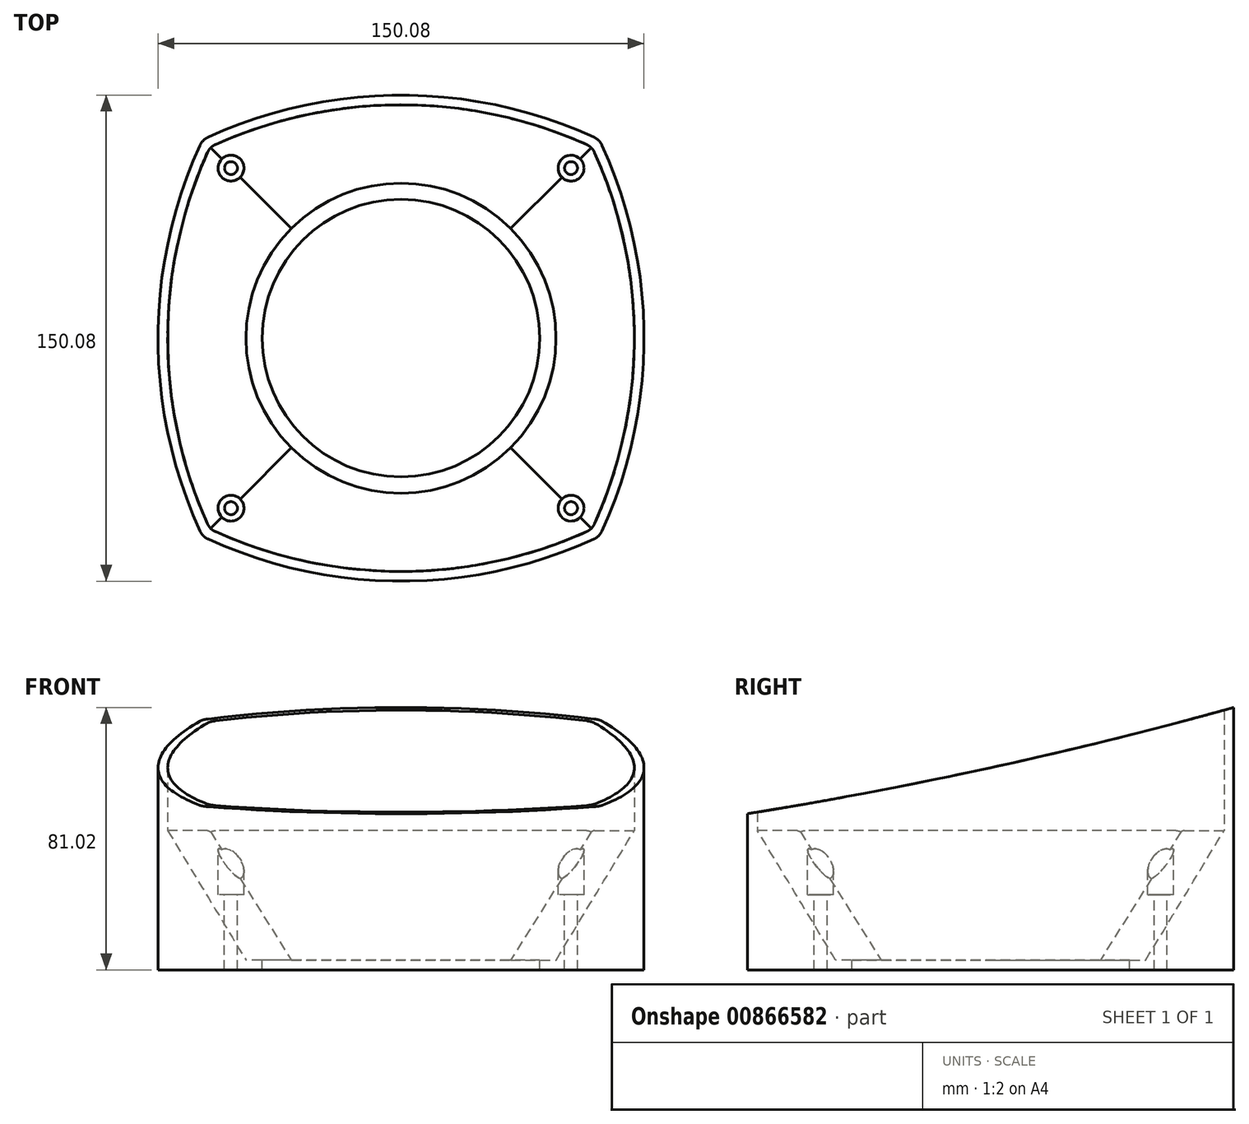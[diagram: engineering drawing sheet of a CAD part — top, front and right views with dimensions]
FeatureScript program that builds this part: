
annotation { "Feature Type Name" : "Feature", "Feature Type Description" : "" }
export const myFeature = defineFeature(function(context is Context, id is Id, definition is map)
    precondition{}
    {
        {
            var Q0;
            Q0=qCreatedBy(makeId("Top.planeOp"),FACE);
            var sketch = newSketch(context, id + "F0", { "sketchPlane" : qUnion([Q0])});
            skLineSegment(sketch, "E0.bottom", {"start": v(196, 49) * mm, "end": v(-196, 49) * mm, "construction": true});
            skLineSegment(sketch, "E0.top", {"start": v(196, -49) * mm, "end": v(-196, -49) * mm, "construction": true});
            skLineSegment(sketch, "E0.left", {"start": v(196, 49) * mm, "end": v(196, -49) * mm, "construction": true});
            skLineSegment(sketch, "E0.right", {"start": v(-196, 49) * mm, "end": v(-196, -49) * mm, "construction": true});
            skPoint(sketch, "E0.middle", {"position": v(0, 0) * mm});
            skLineSegment(sketch, "E1.bottom", {"start": v(207, 59) * mm, "end": v(-207, 59) * mm, "construction": true});
            skLineSegment(sketch, "E1.top", {"start": v(207, -59) * mm, "end": v(-207, -59) * mm, "construction": true});
            skLineSegment(sketch, "E1.left", {"start": v(207, 59) * mm, "end": v(207, -59) * mm, "construction": true});
            skLineSegment(sketch, "E1.right", {"start": v(-207, 59) * mm, "end": v(-207, -59) * mm, "construction": true});
            skLineSegment(sketch, "E2", {"start": v(0, -59) * mm, "end": v(0, 59) * mm, "construction": true});
            skLineSegment(sketch, "E3", {"start": v(-207, 0) * mm, "end": v(207, 0) * mm, "construction": true});
            skCircle(sketch, "E4", {"center": v(0, 0) * mm, "radius": 47.86 * mm});
            skLineSegment(sketch, "E5.bottom", {"start": v(59, 59) * mm, "end": v(-59, 59) * mm, "construction": true});
            skLineSegment(sketch, "E5.top", {"start": v(59, -59) * mm, "end": v(-59, -59) * mm, "construction": true});
            skLineSegment(sketch, "E5.left", {"start": v(59, 59) * mm, "end": v(59, -59) * mm, "construction": true});
            skLineSegment(sketch, "E5.right", {"start": v(-59, 59) * mm, "end": v(-59, -59) * mm, "construction": true});
            skArc(sketch, "E6", {"start": v(59, 59) * mm, "mid": v(0, 72.04) * mm, "end": v(-59, 59) * mm});
            skArc(sketch, "E7", {"start": v(59, -59) * mm, "mid": v(72.04, 0) * mm, "end": v(59, 59) * mm});
            skArc(sketch, "E8", {"start": v(-59, -59) * mm, "mid": v(0, -72.04) * mm, "end": v(59, -59) * mm});
            skArc(sketch, "E9", {"start": v(-59, 59) * mm, "mid": v(-72.04, 0) * mm, "end": v(-59, -59) * mm});
            skArc(sketch, "E10.0", {"start": v(61.26, 61.26) * mm, "mid": v(0, 75.04) * mm, "end": v(-61.26, 61.26) * mm});
            skArc(sketch, "E10.1", {"start": v(61.26, -61.26) * mm, "mid": v(75.04, 0) * mm, "end": v(61.26, 61.26) * mm});
            skArc(sketch, "E10.2", {"start": v(-61.26, -61.26) * mm, "mid": v(0, -75.04) * mm, "end": v(61.26, -61.26) * mm});
            skArc(sketch, "E10.3", {"start": v(-61.26, 61.26) * mm, "mid": v(-75.04, 0) * mm, "end": v(-61.26, -61.26) * mm});
            skSolve(sketch);
        }
        {
            var Q0;
            {var subQ8=sQuery(id+"F0.wireOp",EDGE,"E6");Q0=makeQuery(id+"F0.imprint","IMPRINT",FACE,{"disambiguationData":[TD([[makeQuery(id+"F0.imprint","IMPRINT",EDGE,{"derivedFrom":subQ8}),-1.0]])]});}
            var Q1;
            {var subQ0=sQuery(id+"F0.wireOp",EDGE,"E10.1");var subQ1=sQuery(id+"F0.wireOp",EDGE,"2c3d49d2-39e6-4b7c-b00d-7af9e24e8e71.0");var subQ2=makeQuery(id+"F0.imprint","INTERSECT",VERTEX,{"disambiguationData":[OD(0.0)],"derivedFrom":[subQ1,subQ0]});Q1=makeQuery(id+"F0.imprint","IMPRINT",FACE,{"disambiguationData":[TD([[makeQuery(id+"F0.imprint","IMPRINT",EDGE,{"disambiguationData":[TD([[subQ2,-1.0]])],"derivedFrom":subQ1}),1.0]])]});}
            extrude(context, id + "F1", {"entities" : qUnion([Q0, Q1]), "endBound" : BoundingType.SYMMETRIC, "depth" : 160 * mm, "offsetDistance" : 25 * mm});
        }
        {
            var Q0;
            Q0=qCreatedBy(makeId("Right.planeOp"),FACE);
            var sketch = newSketch(context, id + "F2", { "sketchPlane" : qUnion([Q0])});
            skCircle(sketch, "E11", {"center": v(-294.04, 1407.06) * mm, "radius": 1379.34 * mm});
            skLineSegment(sketch, "E12", {"start": v(0, 0) * mm, "end": v(-237.77, 0) * mm, "construction": true});
            skCircle(sketch, "E13.MirrorC", {"center": v(-294.04, -1407.06) * mm, "radius": 1379.34 * mm});
            skSolve(sketch);
        }
        {
            var Q0;
            Q0=makeQuery(id+"F2.imprint","IMPRINT",FACE,{"disambiguationData":[TD([[makeQuery(id+"F2.imprint","IMPRINT",EDGE,{"derivedFrom":sQuery(id+"F2.wireOp",EDGE,"E11")}),1.0]])]});
            var Q1;
            Q1=makeQuery(id+"F2.imprint","IMPRINT",FACE,{"disambiguationData":[TD([[makeQuery(id+"F2.imprint","IMPRINT",EDGE,{"derivedFrom":sQuery(id+"F2.wireOp",EDGE,"E13.MirrorC")}),-1.0]])]});
            extrude(context, id + "F3", {"entities" : qUnion([Q0, Q1]), "operationType" : NewBodyOperationType.REMOVE, "endBound" : BoundingType.SYMMETRIC, "oppositeDirection" : true, "depth" : 780 * mm, "offsetDistance" : 25 * mm});
        }
        {
            var Q0;
            Q0=qCreatedBy(makeId("Top.planeOp"),FACE);
            cPlane(context, id + "F4", {"entities" : qUnion([Q0]), "cplaneType" : CPlaneType.OFFSET, "offset" : 40 * mm, "width" : 150 * mm, "height" : 150 * mm});
        }
        {
            var Q0;
            Q0=qCreatedBy(id+"F4.planeOp",FACE);
            var sketch = newSketch(context, id + "F5", { "sketchPlane" : qUnion([Q0])});
            skLineSegment(sketch, "E14.bottom", {"start": v(59, 59) * mm, "end": v(-59, 59) * mm, "construction": true});
            skLineSegment(sketch, "E14.top", {"start": v(59, -59) * mm, "end": v(-59, -59) * mm, "construction": true});
            skLineSegment(sketch, "E14.left", {"start": v(59, 59) * mm, "end": v(59, -59) * mm, "construction": true});
            skLineSegment(sketch, "E14.right", {"start": v(-59, 59) * mm, "end": v(-59, -59) * mm, "construction": true});
            skPoint(sketch, "E14.middle", {"position": v(0, 0) * mm});
            skArc(sketch, "E15", {"start": v(59, 59) * mm, "mid": v(0, 72.04) * mm, "end": v(-59, 59) * mm});
            skArc(sketch, "E16", {"start": v(59, -59) * mm, "mid": v(72.04, 0) * mm, "end": v(59, 59) * mm});
            skArc(sketch, "E17", {"start": v(-59, -59) * mm, "mid": v(0, -72.04) * mm, "end": v(59, -59) * mm});
            skArc(sketch, "E18", {"start": v(-59, 59) * mm, "mid": v(-72.04, 0) * mm, "end": v(-59, -59) * mm});
            skSolve(sketch);
        }
        {
            var Q0;
            Q0=qCreatedBy(makeId("Top.planeOp"),FACE);
            var sketch = newSketch(context, id + "F6", { "sketchPlane" : qUnion([Q0])});
            skLineSegment(sketch, "E19.bottom", {"start": v(59, 59) * mm, "end": v(-59, 59) * mm, "construction": true});
            skLineSegment(sketch, "E19.top", {"start": v(59, -59) * mm, "end": v(-59, -59) * mm, "construction": true});
            skLineSegment(sketch, "E19.left", {"start": v(59, 59) * mm, "end": v(59, -59) * mm, "construction": true});
            skLineSegment(sketch, "E19.right", {"start": v(-59, 59) * mm, "end": v(-59, -59) * mm, "construction": true});
            skPoint(sketch, "E19.middle", {"position": v(0, 0) * mm});
            skArc(sketch, "E20", {"start": v(59, 59) * mm, "mid": v(0, 72.04) * mm, "end": v(-59, 59) * mm});
            skArc(sketch, "E21", {"start": v(59, -59) * mm, "mid": v(72.04, 0) * mm, "end": v(59, 59) * mm});
            skArc(sketch, "E22", {"start": v(-59, -59) * mm, "mid": v(0, -72.04) * mm, "end": v(59, -59) * mm});
            skArc(sketch, "E23", {"start": v(-59, 59) * mm, "mid": v(-72.04, 0) * mm, "end": v(-59, -59) * mm});
            skArc(sketch, "E24.0", {"start": v(61.26, 61.26) * mm, "mid": v(0, 75.04) * mm, "end": v(-61.26, 61.26) * mm});
            skArc(sketch, "E24.1", {"start": v(61.26, -61.26) * mm, "mid": v(75.04, 0) * mm, "end": v(61.26, 61.26) * mm});
            skArc(sketch, "E24.2", {"start": v(-61.26, -61.26) * mm, "mid": v(0, -75.04) * mm, "end": v(61.26, -61.26) * mm});
            skArc(sketch, "E24.3", {"start": v(-61.26, 61.26) * mm, "mid": v(-75.04, 0) * mm, "end": v(-61.26, -61.26) * mm});
            skSolve(sketch);
        }
        {
            var Q0;
            Q0=qSketchRegion(id+"F6",true);
            var Q1;
            Q1=makeQuery(id+"F0.imprint","IMPRINT",FACE,{"disambiguationData":[TD([[makeQuery(id+"F0.imprint","IMPRINT",EDGE,{"derivedFrom":sQuery(id+"F0.wireOp",EDGE,"E4")}),-1.0]])]});
            var Q2;
            Q2=makeQuery(id+"F6.imprint","IMPRINT",FACE,{"disambiguationData":[TD([[makeQuery(id+"F6.imprint","IMPRINT",EDGE,{"derivedFrom":sQuery(id+"F6.wireOp",EDGE,"E20")}),1.0]])]});
            extrude(context, id + "F7", {"entities" : qUnion([Q0, Q1, Q2]), "operationType" : NewBodyOperationType.ADD, "endBound" : BoundingType.SYMMETRIC, "depth" : 80 * mm, "offsetDistance" : 25 * mm});
        }
        {
            var Q0;
            Q0=qCreatedBy(makeId("Top.planeOp"),FACE);
            var sketch = newSketch(context, id + "F8", { "sketchPlane" : qUnion([Q0])});
            skCircle(sketch, "E25", {"center": v(0, 0) * mm, "radius": 47.86 * mm});
            skSolve(sketch);
        }
        {
            var Q1;
            Q1=qSketchRegion(id+"F5",true);
            var Q2;
            Q2=qSketchRegion(id+"F8",true);
            loft(context, id + "F9", {"operationType" : NewBodyOperationType.REMOVE, "sheetProfilesArray" : [{ "sheetProfileEntities" : qUnion([Q1]) }, { "sheetProfileEntities" : qUnion([Q2]) }]});
        }
        {
            var Q0;
            Q0=makeQuery(id+"F0.imprint","IMPRINT",FACE,{"disambiguationData":[TD([[makeQuery(id+"F0.imprint","IMPRINT",EDGE,{"derivedFrom":sQuery(id+"F0.wireOp",EDGE,"E4")}),1.0]])]});
            var sketch = newSketch(context, id + "F10", { "sketchPlane" : qUnion([Q0])});
            skCircle(sketch, "E26", {"center": v(0, 0) * mm, "radius": 42.86 * mm});
            skSolve(sketch);
        }
        {
            var Q0;
            Q0=makeQuery(id+"F10.imprint","IMPRINT",FACE,{"disambiguationData":[TD([[makeQuery(id+"F10.imprint","IMPRINT",EDGE,{"derivedFrom":sQuery(id+"F10.wireOp",EDGE,"E26")}),1.0]])]});
            extrude(context, id + "F11", {"entities" : qUnion([Q0]), "operationType" : NewBodyOperationType.REMOVE, "oppositeDirection" : true, "depth" : 3 * mm, "offsetDistance" : 25 * mm});
        }
        {
            var Q0;
            Q0=qCreatedBy(makeId("Top.planeOp"),FACE);
            cPlane(context, id + "F12", {"entities" : qUnion([Q0]), "cplaneType" : CPlaneType.OFFSET, "offset" : 3 * mm, "oppositeDirection" : true, "width" : 150 * mm, "height" : 150 * mm});
        }
        {
            var Q0;
            Q0=qCreatedBy(id+"F12.planeOp",FACE);
            var sketch = newSketch(context, id + "F13", { "sketchPlane" : qUnion([Q0])});
            skLineSegment(sketch, "E27.bottom", {"start": v(59, 59) * mm, "end": v(-59, 59) * mm, "construction": true});
            skLineSegment(sketch, "E27.top", {"start": v(59, -59) * mm, "end": v(-59, -59) * mm, "construction": true});
            skLineSegment(sketch, "E27.left", {"start": v(59, 59) * mm, "end": v(59, -59) * mm, "construction": true});
            skLineSegment(sketch, "E27.right", {"start": v(-59, 59) * mm, "end": v(-59, -59) * mm, "construction": true});
            skPoint(sketch, "E27.middle", {"position": v(0, 0) * mm});
            skArc(sketch, "E28", {"start": v(59, 59) * mm, "mid": v(0, 72.04) * mm, "end": v(-59, 59) * mm});
            skArc(sketch, "E29", {"start": v(59, -59) * mm, "mid": v(72.04, 0) * mm, "end": v(59, 59) * mm});
            skArc(sketch, "E30", {"start": v(-59, -59) * mm, "mid": v(0, -72.04) * mm, "end": v(59, -59) * mm});
            skArc(sketch, "E31", {"start": v(-59, 59) * mm, "mid": v(-72.04, 0) * mm, "end": v(-59, -59) * mm});
            skSolve(sketch);
        }
        {
            var Q0;
            Q0=qSketchRegion(id+"F13",true);
            extrude(context, id + "F14", {"entities" : qUnion([Q0]), "operationType" : NewBodyOperationType.REMOVE, "oppositeDirection" : true, "depth" : 31 * mm, "offsetDistance" : 25 * mm});
        }
        {
            var Q0;
            Q0=makeQuery(id+"F7.boolean.opBoolean","MERGE",FACE,{"derivedFrom":[makeQuery(id+"F7.opExtrude","CAP_FACE",FACE,{"disambiguationData":[OSD([sQuery(id+"F0.wireOp",EDGE,"E4"),sQuery(id+"F0.wireOp",EDGE,"E6"),sQuery(id+"F0.wireOp",EDGE,"E7"),sQuery(id+"F0.wireOp",EDGE,"E8"),sQuery(id+"F0.wireOp",EDGE,"E9")])],"isStart":true}),makeQuery(id+"F7.opExtrude","CAP_FACE",FACE,{"disambiguationData":[OSD([sQuery(id+"F6.wireOp",EDGE,"E24.0"),sQuery(id+"F6.wireOp",EDGE,"E24.1"),sQuery(id+"F6.wireOp",EDGE,"E24.2"),sQuery(id+"F6.wireOp",EDGE,"E24.3")])],"isStart":true})]});
            var sketch = newSketch(context, id + "F15", { "sketchPlane" : qUnion([Q0])});
            skCircle(sketch, "E32", {"center": v(0, 0) * mm, "radius": 62.5 * mm});
            skCircle(sketch, "E33", {"center": v(0, 0) * mm, "radius": 61 * mm});
            skCircle(sketch, "E34", {"center": v(0, 0) * mm, "radius": 57.5 * mm});
            skCircle(sketch, "E35", {"center": v(0, 0) * mm, "radius": 56 * mm});
            skCircle(sketch, "E36", {"center": v(0, 0) * mm, "radius": 52.5 * mm});
            skCircle(sketch, "E37", {"center": v(0, 0) * mm, "radius": 51 * mm});
            skCircle(sketch, "E38", {"center": v(0, 0) * mm, "radius": 47.5 * mm});
            skCircle(sketch, "E39", {"center": v(0, 0) * mm, "radius": 46 * mm});
            skCircle(sketch, "E40", {"center": v(0, 0) * mm, "radius": 42.5 * mm});
            skCircle(sketch, "E41", {"center": v(0, 0) * mm, "radius": 41 * mm});
            skCircle(sketch, "E42", {"center": v(0, 0) * mm, "radius": 37.5 * mm});
            skCircle(sketch, "E43", {"center": v(0, 0) * mm, "radius": 36 * mm});
            skLineSegment(sketch, "E44.bottom", {"start": v(1, -67) * mm, "end": v(-1, -67) * mm});
            skLineSegment(sketch, "E44.top", {"start": v(1, 67) * mm, "end": v(-1, 67) * mm});
            skLineSegment(sketch, "E44.left", {"start": v(1, -67) * mm, "end": v(1, 67) * mm});
            skLineSegment(sketch, "E44.right", {"start": v(-1, -67) * mm, "end": v(-1, 67) * mm});
            skLineSegment(sketch, "E45.bottom", {"start": v(67.5, -1) * mm, "end": v(-67.5, -1) * mm});
            skLineSegment(sketch, "E45.top", {"start": v(67.5, 1) * mm, "end": v(-67.5, 1) * mm});
            skLineSegment(sketch, "E45.left", {"start": v(67.5, -1) * mm, "end": v(67.5, 1) * mm});
            skLineSegment(sketch, "E45.right", {"start": v(-67.5, -1) * mm, "end": v(-67.5, 1) * mm});
            skSolve(sketch);
        }
        {
            var Q0;
            {var subQ0=sQuery(id+"F15.wireOp",EDGE,"E44.right");var subQ1=sQuery(id+"F15.wireOp",EDGE,"E32");var subQ2=makeQuery(id+"F15.imprint","INTERSECT",VERTEX,{"disambiguationData":[OD(0.0)],"derivedFrom":[subQ1,subQ0]});Q0=makeQuery(id+"F15.imprint","IMPRINT",FACE,{"disambiguationData":[TD([[makeQuery(id+"F15.imprint","IMPRINT",EDGE,{"disambiguationData":[TD([[subQ2,-1.0]])],"derivedFrom":subQ1}),1.0]])]});}
            var Q1;
            {var subQ0=sQuery(id+"F15.wireOp",EDGE,"E44.right");var subQ1=sQuery(id+"F15.wireOp",EDGE,"E34");var subQ2=makeQuery(id+"F15.imprint","INTERSECT",VERTEX,{"disambiguationData":[OD(0.0)],"derivedFrom":[subQ1,subQ0]});Q1=makeQuery(id+"F15.imprint","IMPRINT",FACE,{"disambiguationData":[TD([[makeQuery(id+"F15.imprint","IMPRINT",EDGE,{"disambiguationData":[TD([[subQ2,-1.0]])],"derivedFrom":subQ1}),1.0]])]});}
            var Q2;
            {var subQ0=sQuery(id+"F15.wireOp",EDGE,"E44.right");var subQ1=sQuery(id+"F15.wireOp",EDGE,"E36");var subQ2=makeQuery(id+"F15.imprint","INTERSECT",VERTEX,{"disambiguationData":[OD(0.0)],"derivedFrom":[subQ1,subQ0]});Q2=makeQuery(id+"F15.imprint","IMPRINT",FACE,{"disambiguationData":[TD([[makeQuery(id+"F15.imprint","IMPRINT",EDGE,{"disambiguationData":[TD([[subQ2,-1.0]])],"derivedFrom":subQ1}),1.0]])]});}
            var Q3;
            {var subQ0=sQuery(id+"F15.wireOp",EDGE,"E44.right");var subQ1=sQuery(id+"F15.wireOp",EDGE,"E38");var subQ2=makeQuery(id+"F15.imprint","INTERSECT",VERTEX,{"disambiguationData":[OD(0.0)],"derivedFrom":[subQ1,subQ0]});Q3=makeQuery(id+"F15.imprint","IMPRINT",FACE,{"disambiguationData":[TD([[makeQuery(id+"F15.imprint","IMPRINT",EDGE,{"disambiguationData":[TD([[subQ2,-1.0]])],"derivedFrom":subQ1}),1.0]])]});}
            var Q4;
            {var subQ0=sQuery(id+"F15.wireOp",EDGE,"E44.right");var subQ1=sQuery(id+"F15.wireOp",EDGE,"E40");var subQ2=makeQuery(id+"F15.imprint","INTERSECT",VERTEX,{"disambiguationData":[OD(0.0)],"derivedFrom":[subQ1,subQ0]});Q4=makeQuery(id+"F15.imprint","IMPRINT",FACE,{"disambiguationData":[TD([[makeQuery(id+"F15.imprint","IMPRINT",EDGE,{"disambiguationData":[TD([[subQ2,-1.0]])],"derivedFrom":subQ1}),1.0]])]});}
            var Q5;
            {var subQ0=sQuery(id+"F15.wireOp",EDGE,"E44.right");var subQ1=sQuery(id+"F15.wireOp",EDGE,"E42");var subQ2=makeQuery(id+"F15.imprint","INTERSECT",VERTEX,{"disambiguationData":[OD(0.0)],"derivedFrom":[subQ1,subQ0]});Q5=makeQuery(id+"F15.imprint","IMPRINT",FACE,{"disambiguationData":[TD([[makeQuery(id+"F15.imprint","IMPRINT",EDGE,{"disambiguationData":[TD([[subQ2,-1.0]])],"derivedFrom":subQ1}),1.0]])]});}
            var Q6;
            {var subQ0=sQuery(id+"F15.wireOp",EDGE,"E44.left");var subQ1=sQuery(id+"F15.wireOp",EDGE,"E42");var subQ2=makeQuery(id+"F15.imprint","INTERSECT",VERTEX,{"disambiguationData":[OD(0.0)],"derivedFrom":[subQ1,subQ0]});Q6=makeQuery(id+"F15.imprint","IMPRINT",FACE,{"disambiguationData":[TD([[makeQuery(id+"F15.imprint","IMPRINT",EDGE,{"disambiguationData":[TD([[subQ2,1.0]])],"derivedFrom":subQ1}),1.0]])]});}
            var Q7;
            {var subQ0=sQuery(id+"F15.wireOp",EDGE,"E44.left");var subQ1=sQuery(id+"F15.wireOp",EDGE,"E40");var subQ2=makeQuery(id+"F15.imprint","INTERSECT",VERTEX,{"disambiguationData":[OD(0.0)],"derivedFrom":[subQ1,subQ0]});Q7=makeQuery(id+"F15.imprint","IMPRINT",FACE,{"disambiguationData":[TD([[makeQuery(id+"F15.imprint","IMPRINT",EDGE,{"disambiguationData":[TD([[subQ2,1.0]])],"derivedFrom":subQ1}),1.0]])]});}
            var Q8;
            {var subQ0=sQuery(id+"F15.wireOp",EDGE,"E44.left");var subQ1=sQuery(id+"F15.wireOp",EDGE,"E38");var subQ2=makeQuery(id+"F15.imprint","INTERSECT",VERTEX,{"disambiguationData":[OD(0.0)],"derivedFrom":[subQ1,subQ0]});Q8=makeQuery(id+"F15.imprint","IMPRINT",FACE,{"disambiguationData":[TD([[makeQuery(id+"F15.imprint","IMPRINT",EDGE,{"disambiguationData":[TD([[subQ2,1.0]])],"derivedFrom":subQ1}),1.0]])]});}
            var Q9;
            {var subQ0=sQuery(id+"F15.wireOp",EDGE,"E44.left");var subQ1=sQuery(id+"F15.wireOp",EDGE,"E36");var subQ2=makeQuery(id+"F15.imprint","INTERSECT",VERTEX,{"disambiguationData":[OD(0.0)],"derivedFrom":[subQ1,subQ0]});Q9=makeQuery(id+"F15.imprint","IMPRINT",FACE,{"disambiguationData":[TD([[makeQuery(id+"F15.imprint","IMPRINT",EDGE,{"disambiguationData":[TD([[subQ2,1.0]])],"derivedFrom":subQ1}),1.0]])]});}
            var Q10;
            {var subQ0=sQuery(id+"F15.wireOp",EDGE,"E44.left");var subQ1=sQuery(id+"F15.wireOp",EDGE,"E34");var subQ2=makeQuery(id+"F15.imprint","INTERSECT",VERTEX,{"disambiguationData":[OD(0.0)],"derivedFrom":[subQ1,subQ0]});Q10=makeQuery(id+"F15.imprint","IMPRINT",FACE,{"disambiguationData":[TD([[makeQuery(id+"F15.imprint","IMPRINT",EDGE,{"disambiguationData":[TD([[subQ2,1.0]])],"derivedFrom":subQ1}),1.0]])]});}
            var Q11;
            {var subQ0=sQuery(id+"F15.wireOp",EDGE,"E44.left");var subQ1=sQuery(id+"F15.wireOp",EDGE,"E32");var subQ2=makeQuery(id+"F15.imprint","INTERSECT",VERTEX,{"disambiguationData":[OD(0.0)],"derivedFrom":[subQ1,subQ0]});Q11=makeQuery(id+"F15.imprint","IMPRINT",FACE,{"disambiguationData":[TD([[makeQuery(id+"F15.imprint","IMPRINT",EDGE,{"disambiguationData":[TD([[subQ2,1.0]])],"derivedFrom":subQ1}),1.0]])]});}
            var Q12;
            {var subQ0=sQuery(id+"F15.wireOp",EDGE,"E44.left");var subQ1=sQuery(id+"F15.wireOp",EDGE,"E42");var subQ2=makeQuery(id+"F15.imprint","INTERSECT",VERTEX,{"disambiguationData":[OD(1.0)],"derivedFrom":[subQ1,subQ0]});Q12=makeQuery(id+"F15.imprint","IMPRINT",FACE,{"disambiguationData":[TD([[makeQuery(id+"F15.imprint","IMPRINT",EDGE,{"disambiguationData":[TD([[subQ2,-1.0]])],"derivedFrom":subQ1}),1.0]])]});}
            var Q13;
            {var subQ0=sQuery(id+"F15.wireOp",EDGE,"E45.bottom");var subQ1=sQuery(id+"F15.wireOp",EDGE,"E42");var subQ2=makeQuery(id+"F15.imprint","INTERSECT",VERTEX,{"disambiguationData":[OD(0.0)],"derivedFrom":[subQ1,subQ0]});Q13=makeQuery(id+"F15.imprint","IMPRINT",FACE,{"disambiguationData":[TD([[makeQuery(id+"F15.imprint","IMPRINT",EDGE,{"disambiguationData":[TD([[subQ2,-1.0]])],"derivedFrom":subQ1}),1.0]])]});}
            var Q14;
            {var subQ0=sQuery(id+"F15.wireOp",EDGE,"E45.bottom");var subQ1=sQuery(id+"F15.wireOp",EDGE,"E40");var subQ2=makeQuery(id+"F15.imprint","INTERSECT",VERTEX,{"disambiguationData":[OD(0.0)],"derivedFrom":[subQ1,subQ0]});Q14=makeQuery(id+"F15.imprint","IMPRINT",FACE,{"disambiguationData":[TD([[makeQuery(id+"F15.imprint","IMPRINT",EDGE,{"disambiguationData":[TD([[subQ2,-1.0]])],"derivedFrom":subQ1}),1.0]])]});}
            var Q15;
            {var subQ0=sQuery(id+"F15.wireOp",EDGE,"E44.left");var subQ1=sQuery(id+"F15.wireOp",EDGE,"E40");var subQ2=makeQuery(id+"F15.imprint","INTERSECT",VERTEX,{"disambiguationData":[OD(1.0)],"derivedFrom":[subQ1,subQ0]});Q15=makeQuery(id+"F15.imprint","IMPRINT",FACE,{"disambiguationData":[TD([[makeQuery(id+"F15.imprint","IMPRINT",EDGE,{"disambiguationData":[TD([[subQ2,-1.0]])],"derivedFrom":subQ1}),1.0]])]});}
            var Q16;
            {var subQ0=sQuery(id+"F15.wireOp",EDGE,"E44.left");var subQ1=sQuery(id+"F15.wireOp",EDGE,"E38");var subQ2=makeQuery(id+"F15.imprint","INTERSECT",VERTEX,{"disambiguationData":[OD(1.0)],"derivedFrom":[subQ1,subQ0]});Q16=makeQuery(id+"F15.imprint","IMPRINT",FACE,{"disambiguationData":[TD([[makeQuery(id+"F15.imprint","IMPRINT",EDGE,{"disambiguationData":[TD([[subQ2,-1.0]])],"derivedFrom":subQ1}),1.0]])]});}
            var Q17;
            {var subQ0=sQuery(id+"F15.wireOp",EDGE,"E45.bottom");var subQ1=sQuery(id+"F15.wireOp",EDGE,"E38");var subQ2=makeQuery(id+"F15.imprint","INTERSECT",VERTEX,{"disambiguationData":[OD(0.0)],"derivedFrom":[subQ1,subQ0]});Q17=makeQuery(id+"F15.imprint","IMPRINT",FACE,{"disambiguationData":[TD([[makeQuery(id+"F15.imprint","IMPRINT",EDGE,{"disambiguationData":[TD([[subQ2,-1.0]])],"derivedFrom":subQ1}),1.0]])]});}
            var Q18;
            {var subQ0=sQuery(id+"F15.wireOp",EDGE,"E45.bottom");var subQ1=sQuery(id+"F15.wireOp",EDGE,"E36");var subQ2=makeQuery(id+"F15.imprint","INTERSECT",VERTEX,{"disambiguationData":[OD(0.0)],"derivedFrom":[subQ1,subQ0]});Q18=makeQuery(id+"F15.imprint","IMPRINT",FACE,{"disambiguationData":[TD([[makeQuery(id+"F15.imprint","IMPRINT",EDGE,{"disambiguationData":[TD([[subQ2,-1.0]])],"derivedFrom":subQ1}),1.0]])]});}
            var Q19;
            {var subQ0=sQuery(id+"F15.wireOp",EDGE,"E44.left");var subQ1=sQuery(id+"F15.wireOp",EDGE,"E36");var subQ2=makeQuery(id+"F15.imprint","INTERSECT",VERTEX,{"disambiguationData":[OD(1.0)],"derivedFrom":[subQ1,subQ0]});Q19=makeQuery(id+"F15.imprint","IMPRINT",FACE,{"disambiguationData":[TD([[makeQuery(id+"F15.imprint","IMPRINT",EDGE,{"disambiguationData":[TD([[subQ2,-1.0]])],"derivedFrom":subQ1}),1.0]])]});}
            var Q20;
            {var subQ0=sQuery(id+"F15.wireOp",EDGE,"E44.left");var subQ1=sQuery(id+"F15.wireOp",EDGE,"E34");var subQ2=makeQuery(id+"F15.imprint","INTERSECT",VERTEX,{"disambiguationData":[OD(1.0)],"derivedFrom":[subQ1,subQ0]});Q20=makeQuery(id+"F15.imprint","IMPRINT",FACE,{"disambiguationData":[TD([[makeQuery(id+"F15.imprint","IMPRINT",EDGE,{"disambiguationData":[TD([[subQ2,-1.0]])],"derivedFrom":subQ1}),1.0]])]});}
            var Q21;
            {var subQ0=sQuery(id+"F15.wireOp",EDGE,"E45.bottom");var subQ1=sQuery(id+"F15.wireOp",EDGE,"E34");var subQ2=makeQuery(id+"F15.imprint","INTERSECT",VERTEX,{"disambiguationData":[OD(0.0)],"derivedFrom":[subQ1,subQ0]});Q21=makeQuery(id+"F15.imprint","IMPRINT",FACE,{"disambiguationData":[TD([[makeQuery(id+"F15.imprint","IMPRINT",EDGE,{"disambiguationData":[TD([[subQ2,-1.0]])],"derivedFrom":subQ1}),1.0]])]});}
            var Q22;
            {var subQ0=sQuery(id+"F15.wireOp",EDGE,"E45.bottom");var subQ1=sQuery(id+"F15.wireOp",EDGE,"E32");var subQ2=makeQuery(id+"F15.imprint","INTERSECT",VERTEX,{"disambiguationData":[OD(0.0)],"derivedFrom":[subQ1,subQ0]});Q22=makeQuery(id+"F15.imprint","IMPRINT",FACE,{"disambiguationData":[TD([[makeQuery(id+"F15.imprint","IMPRINT",EDGE,{"disambiguationData":[TD([[subQ2,-1.0]])],"derivedFrom":subQ1}),1.0]])]});}
            var Q23;
            {var subQ0=sQuery(id+"F15.wireOp",EDGE,"E44.left");var subQ1=sQuery(id+"F15.wireOp",EDGE,"E32");var subQ2=makeQuery(id+"F15.imprint","INTERSECT",VERTEX,{"disambiguationData":[OD(1.0)],"derivedFrom":[subQ1,subQ0]});Q23=makeQuery(id+"F15.imprint","IMPRINT",FACE,{"disambiguationData":[TD([[makeQuery(id+"F15.imprint","IMPRINT",EDGE,{"disambiguationData":[TD([[subQ2,-1.0]])],"derivedFrom":subQ1}),1.0]])]});}
            extrude(context, id + "F16", {"entities" : qUnion([Q0, Q1, Q2, Q3, Q4, Q5, Q6, Q7, Q8, Q9, Q10, Q11, Q12, Q13, Q14, Q15, Q16, Q17, Q18, Q19, Q20, Q21, Q22, Q23]), "operationType" : NewBodyOperationType.REMOVE, "oppositeDirection" : true, "depth" : 25 * mm, "offsetDistance" : 25 * mm});
        }
        {
            var Q0;
            Q0=makeQuery(id+"F1.opExtrude","SWEPT_EDGE",EDGE,{"disambiguationData":[OSD([sQuery(id+"F0.wireOp",EDGE,"E10.0"),sQuery(id+"F0.wireOp",EDGE,"E10.3")])]});
            var Q1;
            Q1=makeQuery(id+"F1.opExtrude","SWEPT_EDGE",EDGE,{"disambiguationData":[OSD([sQuery(id+"F0.wireOp",EDGE,"E10.2"),sQuery(id+"F0.wireOp",EDGE,"E10.3")])]});
            var Q2;
            Q2=makeQuery(id+"F1.opExtrude","SWEPT_EDGE",EDGE,{"disambiguationData":[OSD([sQuery(id+"F0.wireOp",EDGE,"E10.0"),sQuery(id+"F0.wireOp",EDGE,"E10.1")])]});
            var Q3;
            Q3=makeQuery(id+"F1.opExtrude","SWEPT_EDGE",EDGE,{"disambiguationData":[OSD([sQuery(id+"F0.wireOp",EDGE,"E10.1"),sQuery(id+"F0.wireOp",EDGE,"E10.2")])]});
            var Q4;
            {var subQ0=sQuery(id+"F0.wireOp",EDGE,"E9");var subQ1=sQuery(id+"F0.wireOp",EDGE,"E6");Q4=makeQuery(id+"F7.boolean.opBoolean","SPLIT",EDGE,{"disambiguationData":[TD([makeQuery(id+"F3.boolean.opBoolean","COPY",FACE,{"derivedFrom":makeQuery(id+"F3.opExtrude","SWEPT_FACE",FACE,{"disambiguationData":[OSD([sQuery(id+"F2.wireOp",EDGE,"E11")])]})})])],"derivedFrom":makeQuery(id+"F1.opExtrude","SWEPT_EDGE",EDGE,{"disambiguationData":[OSD([subQ1,subQ0])]})});}
            var Q5;
            {var subQ0=sQuery(id+"F0.wireOp",EDGE,"E7");var subQ1=sQuery(id+"F0.wireOp",EDGE,"E6");Q5=makeQuery(id+"F7.boolean.opBoolean","SPLIT",EDGE,{"disambiguationData":[TD([makeQuery(id+"F3.boolean.opBoolean","COPY",FACE,{"derivedFrom":makeQuery(id+"F3.opExtrude","SWEPT_FACE",FACE,{"disambiguationData":[OSD([sQuery(id+"F2.wireOp",EDGE,"E11")])]})})])],"derivedFrom":makeQuery(id+"F1.opExtrude","SWEPT_EDGE",EDGE,{"disambiguationData":[OSD([subQ1,subQ0])]})});}
            var Q6;
            {var subQ0=sQuery(id+"F0.wireOp",EDGE,"E9");var subQ1=sQuery(id+"F0.wireOp",EDGE,"E8");Q6=makeQuery(id+"F7.boolean.opBoolean","SPLIT",EDGE,{"disambiguationData":[TD([makeQuery(id+"F3.boolean.opBoolean","COPY",FACE,{"derivedFrom":makeQuery(id+"F3.opExtrude","SWEPT_FACE",FACE,{"disambiguationData":[OSD([sQuery(id+"F2.wireOp",EDGE,"E11")])]})})])],"derivedFrom":makeQuery(id+"F1.opExtrude","SWEPT_EDGE",EDGE,{"disambiguationData":[OSD([subQ1,subQ0])]})});}
            var Q7;
            {var subQ0=sQuery(id+"F0.wireOp",EDGE,"E8");var subQ1=sQuery(id+"F0.wireOp",EDGE,"E7");Q7=makeQuery(id+"F7.boolean.opBoolean","SPLIT",EDGE,{"disambiguationData":[TD([makeQuery(id+"F3.boolean.opBoolean","COPY",FACE,{"derivedFrom":makeQuery(id+"F3.opExtrude","SWEPT_FACE",FACE,{"disambiguationData":[OSD([sQuery(id+"F2.wireOp",EDGE,"E11")])]})})])],"derivedFrom":makeQuery(id+"F1.opExtrude","SWEPT_EDGE",EDGE,{"disambiguationData":[OSD([subQ1,subQ0])]})});}
            var Q8;
            {var subQ0=sQuery(id+"F0.wireOp",EDGE,"E8");var subQ1=sQuery(id+"F0.wireOp",EDGE,"E7");Q8=makeQuery(id+"F7.boolean.opBoolean","SPLIT",EDGE,{"disambiguationData":[TD([makeQuery(id+"F3.boolean.opBoolean","COPY",FACE,{"derivedFrom":makeQuery(id+"F3.opExtrude","SWEPT_FACE",FACE,{"disambiguationData":[OSD([sQuery(id+"F2.wireOp",EDGE,"E13.MirrorC")])]})})])],"derivedFrom":makeQuery(id+"F1.opExtrude","SWEPT_EDGE",EDGE,{"disambiguationData":[OSD([subQ1,subQ0])]})});}
            var Q9;
            {var subQ0=sQuery(id+"F0.wireOp",EDGE,"E9");var subQ1=sQuery(id+"F0.wireOp",EDGE,"E8");Q9=makeQuery(id+"F7.boolean.opBoolean","SPLIT",EDGE,{"disambiguationData":[TD([makeQuery(id+"F3.boolean.opBoolean","COPY",FACE,{"derivedFrom":makeQuery(id+"F3.opExtrude","SWEPT_FACE",FACE,{"disambiguationData":[OSD([sQuery(id+"F2.wireOp",EDGE,"E13.MirrorC")])]})})])],"derivedFrom":makeQuery(id+"F1.opExtrude","SWEPT_EDGE",EDGE,{"disambiguationData":[OSD([subQ1,subQ0])]})});}
            var Q10;
            {var subQ0=sQuery(id+"F0.wireOp",EDGE,"E9");var subQ1=sQuery(id+"F0.wireOp",EDGE,"E6");Q10=makeQuery(id+"F7.boolean.opBoolean","SPLIT",EDGE,{"disambiguationData":[TD([makeQuery(id+"F3.boolean.opBoolean","COPY",FACE,{"derivedFrom":makeQuery(id+"F3.opExtrude","SWEPT_FACE",FACE,{"disambiguationData":[OSD([sQuery(id+"F2.wireOp",EDGE,"E13.MirrorC")])]})})])],"derivedFrom":makeQuery(id+"F1.opExtrude","SWEPT_EDGE",EDGE,{"disambiguationData":[OSD([subQ1,subQ0])]})});}
            var Q11;
            {var subQ0=sQuery(id+"F0.wireOp",EDGE,"E7");var subQ1=sQuery(id+"F0.wireOp",EDGE,"E6");Q11=makeQuery(id+"F7.boolean.opBoolean","SPLIT",EDGE,{"disambiguationData":[TD([makeQuery(id+"F3.boolean.opBoolean","COPY",FACE,{"derivedFrom":makeQuery(id+"F3.opExtrude","SWEPT_FACE",FACE,{"disambiguationData":[OSD([sQuery(id+"F2.wireOp",EDGE,"E13.MirrorC")])]})})])],"derivedFrom":makeQuery(id+"F1.opExtrude","SWEPT_EDGE",EDGE,{"disambiguationData":[OSD([subQ1,subQ0])]})});}
            fillet(context, id + "F17", {"entities" : qUnion([Q0, Q1, Q2, Q3, Q4, Q5, Q6, Q7, Q8, Q9, Q10, Q11]), "radius" : 5 * mm, "tangentPropagation" : true, "allowEdgeOverflow" : false});
        }
        {
            var Q0;
            Q0=qCreatedBy(makeId("Top.planeOp"),FACE);
            cPlane(context, id + "F18", {"entities" : qUnion([Q0]), "cplaneType" : CPlaneType.OFFSET, "offset" : 50 * mm, "width" : 150 * mm, "height" : 150 * mm});
        }
        {
            var Q0;
            Q0=qCreatedBy(id+"F18.planeOp",FACE);
            var sketch = newSketch(context, id + "F19", { "sketchPlane" : qUnion([Q0])});
            skLineSegment(sketch, "E46.bottom", {"start": v(52.5, 52.5) * mm, "end": v(-52.5, 52.5) * mm, "construction": true});
            skLineSegment(sketch, "E46.top", {"start": v(52.5, -52.5) * mm, "end": v(-52.5, -52.5) * mm, "construction": true});
            skLineSegment(sketch, "E46.left", {"start": v(52.5, 52.5) * mm, "end": v(52.5, -52.5) * mm, "construction": true});
            skLineSegment(sketch, "E46.right", {"start": v(-52.5, 52.5) * mm, "end": v(-52.5, -52.5) * mm, "construction": true});
            skPoint(sketch, "E46.middle", {"position": v(0, 0) * mm});
            skCircle(sketch, "E47", {"center": v(-52.5, 52.5) * mm, "radius": 2 * mm});
            skCircle(sketch, "E48", {"center": v(52.5, 52.5) * mm, "radius": 2 * mm});
            skCircle(sketch, "E49", {"center": v(52.5, -52.5) * mm, "radius": 2 * mm});
            skCircle(sketch, "E50", {"center": v(-52.5, -52.5) * mm, "radius": 2 * mm});
            skSolve(sketch);
        }
        {
            var Q0;
            Q0=sQuery(id+"F19.wireOp",VERTEX,"E46.bottom.end");
            var Q1;
            Q1=sQuery(id+"F19.wireOp",VERTEX,"E46.bottom.start");
            var Q2;
            Q2=sQuery(id+"F19.wireOp",VERTEX,"E46.top.start");
            var Q3;
            Q3=sQuery(id+"F19.wireOp",VERTEX,"E46.top.end");
            var Q4;
            Q4=makeQuery(id+"F1.opExtrude","SWEPT_BODY",BODY,{"disambiguationData":[OSD([sQuery(id+"F0.wireOp",EDGE,"E6"),sQuery(id+"F0.wireOp",EDGE,"E7"),sQuery(id+"F0.wireOp",EDGE,"E8"),sQuery(id+"F0.wireOp",EDGE,"E9"),sQuery(id+"F0.wireOp",EDGE,"E10.0"),sQuery(id+"F0.wireOp",EDGE,"E10.1"),sQuery(id+"F0.wireOp",EDGE,"E10.2"),sQuery(id+"F0.wireOp",EDGE,"E10.3")])]});
            hole(context, id + "F20", {"style" : HoleStyle.C_BORE, "endStyle" : HoleEndStyle.THROUGH, "holeDiameter" : 4 * mm, "cBoreDiameter" : 8 * mm, "cBoreDepth" : 5 * mm, "majorDiameter" : 5 * mm, "isTappedThrough" : true, "tappedDepth" : 12 * mm, "tapClearance" : 3, "locations" : qUnion([Q0, Q1, Q2, Q3]), "scope" : qUnion([Q4])});
        }
        {
            var Q0;
            Q0=makeQuery(id+"F7.boolean.opBoolean","MERGE",FACE,{"derivedFrom":[makeQuery(id+"F7.opExtrude","CAP_FACE",FACE,{"disambiguationData":[OSD([sQuery(id+"F0.wireOp",EDGE,"E4"),sQuery(id+"F0.wireOp",EDGE,"E6"),sQuery(id+"F0.wireOp",EDGE,"E7"),sQuery(id+"F0.wireOp",EDGE,"E8"),sQuery(id+"F0.wireOp",EDGE,"E9")])],"isStart":true}),makeQuery(id+"F7.opExtrude","CAP_FACE",FACE,{"disambiguationData":[OSD([sQuery(id+"F6.wireOp",EDGE,"E24.0"),sQuery(id+"F6.wireOp",EDGE,"E24.1"),sQuery(id+"F6.wireOp",EDGE,"E24.2"),sQuery(id+"F6.wireOp",EDGE,"E24.3")])],"isStart":true})]});
            var sketch = newSketch(context, id + "F21", { "sketchPlane" : qUnion([Q0])});
            skCircle(sketch, "E51.cCircle", {"center": v(-52.5, 52.5) * mm, "radius": 3 * mm, "construction": true});
            skLineSegment(sketch, "E51.0", {"start": v(-54.23, 55.5) * mm, "end": v(-50.77, 55.5) * mm});
            skLineSegment(sketch, "E51.1", {"start": v(-50.77, 55.5) * mm, "end": v(-49.04, 52.5) * mm});
            skLineSegment(sketch, "E51.2", {"start": v(-49.04, 52.5) * mm, "end": v(-50.77, 49.5) * mm});
            skLineSegment(sketch, "E51.3", {"start": v(-50.77, 49.5) * mm, "end": v(-54.23, 49.5) * mm});
            skLineSegment(sketch, "E51.4", {"start": v(-54.23, 49.5) * mm, "end": v(-55.96, 52.5) * mm});
            skLineSegment(sketch, "E51.5", {"start": v(-55.96, 52.5) * mm, "end": v(-54.23, 55.5) * mm});
            skPoint(sketch, "E51.0.midPoint", {"position": v(-52.5, 55.5) * mm});
            skCircle(sketch, "E52.cCircle", {"center": v(52.5, 52.5) * mm, "radius": 3 * mm, "construction": true});
            skLineSegment(sketch, "E52.0", {"start": v(50.77, 55.5) * mm, "end": v(54.23, 55.5) * mm});
            skLineSegment(sketch, "E52.1", {"start": v(54.23, 55.5) * mm, "end": v(55.96, 52.5) * mm});
            skLineSegment(sketch, "E52.2", {"start": v(55.96, 52.5) * mm, "end": v(54.23, 49.5) * mm});
            skLineSegment(sketch, "E52.3", {"start": v(54.23, 49.5) * mm, "end": v(50.77, 49.5) * mm});
            skLineSegment(sketch, "E52.4", {"start": v(50.77, 49.5) * mm, "end": v(49.04, 52.5) * mm});
            skLineSegment(sketch, "E52.5", {"start": v(49.04, 52.5) * mm, "end": v(50.77, 55.5) * mm});
            skPoint(sketch, "E52.0.midPoint", {"position": v(52.5, 55.5) * mm});
            skCircle(sketch, "E53.cCircle", {"center": v(52.5, -52.5) * mm, "radius": 3 * mm, "construction": true});
            skLineSegment(sketch, "E53.0", {"start": v(50.77, -49.5) * mm, "end": v(54.23, -49.5) * mm});
            skLineSegment(sketch, "E53.1", {"start": v(54.23, -49.5) * mm, "end": v(55.96, -52.5) * mm});
            skLineSegment(sketch, "E53.2", {"start": v(55.96, -52.5) * mm, "end": v(54.23, -55.5) * mm});
            skLineSegment(sketch, "E53.3", {"start": v(54.23, -55.5) * mm, "end": v(50.77, -55.5) * mm});
            skLineSegment(sketch, "E53.4", {"start": v(50.77, -55.5) * mm, "end": v(49.04, -52.5) * mm});
            skLineSegment(sketch, "E53.5", {"start": v(49.04, -52.5) * mm, "end": v(50.77, -49.5) * mm});
            skPoint(sketch, "E53.0.midPoint", {"position": v(52.5, -49.5) * mm});
            skCircle(sketch, "E54.cCircle", {"center": v(-52.5, -52.5) * mm, "radius": 3 * mm, "construction": true});
            skLineSegment(sketch, "E54.0", {"start": v(-54.23, -49.5) * mm, "end": v(-50.77, -49.5) * mm});
            skLineSegment(sketch, "E54.1", {"start": v(-50.77, -49.5) * mm, "end": v(-49.04, -52.5) * mm});
            skLineSegment(sketch, "E54.2", {"start": v(-49.04, -52.5) * mm, "end": v(-50.77, -55.5) * mm});
            skLineSegment(sketch, "E54.3", {"start": v(-50.77, -55.5) * mm, "end": v(-54.23, -55.5) * mm});
            skLineSegment(sketch, "E54.4", {"start": v(-54.23, -55.5) * mm, "end": v(-55.96, -52.5) * mm});
            skLineSegment(sketch, "E54.5", {"start": v(-55.96, -52.5) * mm, "end": v(-54.23, -49.5) * mm});
            skPoint(sketch, "E54.0.midPoint", {"position": v(-52.5, -49.5) * mm});
            skSolve(sketch);
        }
        {
            var Q0;
            Q0=makeQuery(id+"F21.imprint","IMPRINT",FACE,{"disambiguationData":[TD([[makeQuery(id+"F21.imprint","IMPRINT",EDGE,{"derivedFrom":sQuery(id+"F21.wireOp",EDGE,"E51.0")}),-1.0]])]});
            var Q1;
            Q1=makeQuery(id+"F21.imprint","IMPRINT",FACE,{"disambiguationData":[TD([[makeQuery(id+"F21.imprint","IMPRINT",EDGE,{"derivedFrom":sQuery(id+"F21.wireOp",EDGE,"E52.0")}),-1.0]])]});
            var Q2;
            Q2=makeQuery(id+"F21.imprint","IMPRINT",FACE,{"disambiguationData":[TD([[makeQuery(id+"F21.imprint","IMPRINT",EDGE,{"derivedFrom":sQuery(id+"F21.wireOp",EDGE,"E53.0")}),-1.0]])]});
            var Q3;
            Q3=makeQuery(id+"F21.imprint","IMPRINT",FACE,{"disambiguationData":[TD([[makeQuery(id+"F21.imprint","IMPRINT",EDGE,{"derivedFrom":sQuery(id+"F21.wireOp",EDGE,"E54.0")}),-1.0]])]});
            extrude(context, id + "F22", {"entities" : qUnion([Q0, Q1, Q2, Q3]), "operationType" : NewBodyOperationType.REMOVE, "oppositeDirection" : true, "depth" : 3 * mm, "offsetDistance" : 25 * mm});
        }
        {
            var Q0;
            Q0=qCreatedBy(makeId("Right.planeOp"),FACE);
            var sketch = newSketch(context, id + "F23", { "sketchPlane" : qUnion([Q0])});
            skCircle(sketch, "E55", {"center": v(-40, -20) * mm, "radius": 12.5 * mm});
            skSolve(sketch);
        }
        {
            var Q0;
            Q0=qSketchRegion(id+"F23",true);
            extrude(context, id + "F24", {"entities" : qUnion([Q0]), "operationType" : NewBodyOperationType.REMOVE, "depth" : 249 * mm, "offsetDistance" : 25 * mm});
        }
        {
            var Q0;
            Q0=qCreatedBy(id+"F12.planeOp",FACE);
            var sketch = newSketch(context, id + "F25", { "sketchPlane" : qUnion([Q0])});
            skCircle(sketch, "E56", {"center": v(0, 0) * mm, "radius": 125 * mm});
            skSolve(sketch);
        }
        {
            var Q0;
            Q0 = qSketchRegion(id + "F25", true);
            extrude(context, id + "F26", {"entities" : qUnion([Q0]), "operationType" : NewBodyOperationType.REMOVE, "oppositeDirection" : true, "depth" : 125 * mm, "offsetDistance" : 25 * mm});
        }
    });
